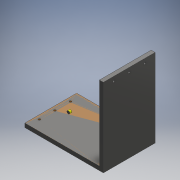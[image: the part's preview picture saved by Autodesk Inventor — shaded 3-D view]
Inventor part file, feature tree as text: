
AUTODESK INVENTOR PART (.ipt)
format: ipt  version: 2016 (Build 200138000, 138)  size: 132,608 bytes
history: native  units: mm
features: hole x6, extrude x2, sketch x2, thicken_offset x1, other x1
ambient origin geometry x8: Origin, YZ Plane, XZ Plane, XY Plane, X Axis, Y Axis, Z Axis, Center Point
bodies: Solid1 (feature_tree), Solid2 (feature_tree)
feature tree (12):
  thicken_offset  "Thicken1"
  hole  "Hole1"  [1 undecoded]
  hole  "Hole2"  [1 undecoded]
  hole  "Hole3"  [1 undecoded]
  hole  "Hole4"  [1 undecoded]
  hole  "Hole5"  [1 undecoded]
  hole  "Hole6"  [1 undecoded]
  extrude  "Extrusion1"  Depth=10.0mm
  sketch  "Sketch1"  dims[d0=360.0mm d1=90.0deg]
  other  "Srf1"
  sketch  "Sketch3"  dims[d2=360.0mm d7=250.0mm d8=0.0mm d9=19.0mm d10=19.0mm d18=50.0mm d19=20.0mm d20=10.0mm d21=6.0mm d22=4.0mm d23=2.0mm d24=90.0deg d25=8.0mm d26=20.594885mm d27=125.0mm d28=20.0mm d29=10.0mm d30=6.0mm d31=4.0mm d32=2.0mm d33=90.0deg d34=8.0mm d35=20.594885mm d36=20.0mm d37=50.0mm d38=10.0mm d39=6.0mm d40=4.0mm d41=2.0mm d42=90.0deg d43=8.0mm d44=20.594885mm d45=50.0mm d46=20.0mm d47=10.0mm d48=6.0mm d49=4.0mm d50=2.0mm d51=90.0deg d52=8.0mm d53=20.594885mm d54=20.0mm d55=125.0mm d56=10.0mm d57=6.0mm d58=4.0mm d59=2.0mm d60=90.0deg d61=8.0mm d62=20.594885mm d63=20.0mm d64=50.0mm d65=10.0mm d66=6.0mm d67=4.0mm d68=2.0mm d69=90.0deg d70=8.0mm d71=20.594885mm d75=150.0mm d76=150.0mm d77=10.0mm d78=0.0mm]
  extrude  "ExtrusionSrf1"  Depth=10.0mm
note: 6 required parameter values undecoded (feature->parameter linkage not recoverable at this tier; creation-order binding heuristic only, values carry confidence <= 0.55)
